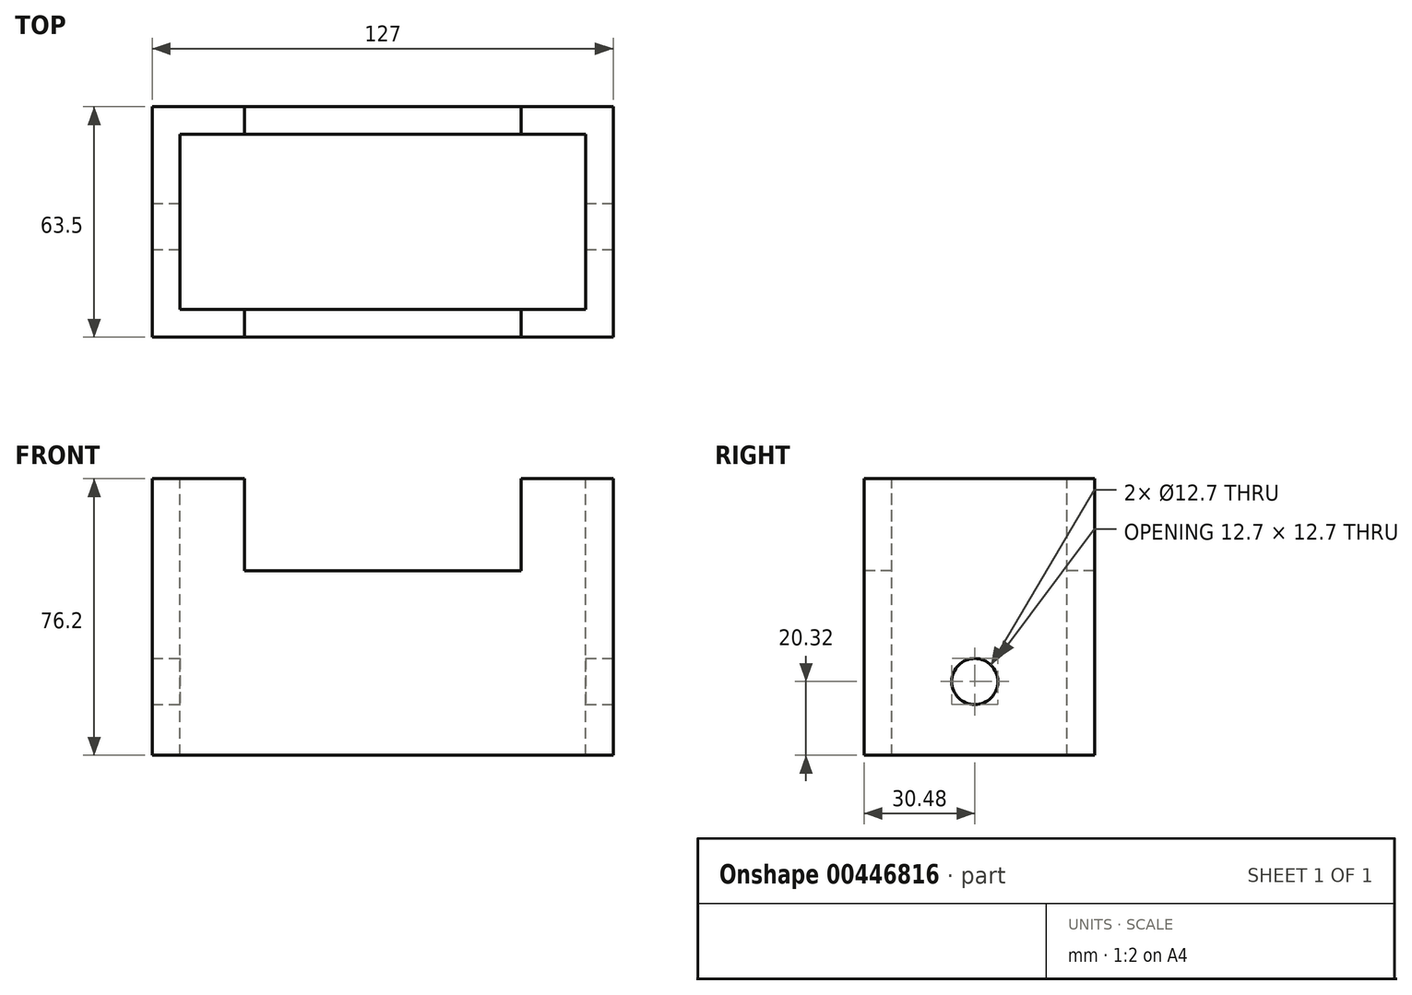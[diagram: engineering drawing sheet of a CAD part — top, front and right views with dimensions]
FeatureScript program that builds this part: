
annotation { "Feature Type Name" : "Feature", "Feature Type Description" : "" }
export const myFeature = defineFeature(function(context is Context, id is Id, definition is map)
    precondition{}
    {
        {
            var Q0;
            Q0=qCreatedBy(makeId("Front.planeOp"),FACE);
            var sketch = newSketch(context, id + "F0", { "sketchPlane" : qUnion([Q0])});
            skLineSegment(sketch, "E0.bottom", {"start": v(-63.5, 38.1) * mm, "end": v(63.5, 38.1) * mm});
            skLineSegment(sketch, "E0.top", {"start": v(-63.5, -38.1) * mm, "end": v(63.5, -38.1) * mm});
            skLineSegment(sketch, "E0.left", {"start": v(-63.5, 38.1) * mm, "end": v(-63.5, -38.1) * mm});
            skLineSegment(sketch, "E0.right", {"start": v(63.5, 38.1) * mm, "end": v(63.5, -38.1) * mm});
            skSolve(sketch);
        }
        {
            var Q0;
            Q0 = qSketchRegion(id + "F0", true);
            extrude(context, id + "F1", {"entities" : qUnion([Q0]), "depth" : 63.5 * mm});
        }
        {
            var Q0;
            Q0=makeQuery(id+"F1.opExtrude","CAP_FACE",FACE,{"disambiguationData":[OSD([sQuery(id+"F0.wireOp",EDGE,"E0.bottom"),sQuery(id+"F0.wireOp",EDGE,"E0.top"),sQuery(id+"F0.wireOp",EDGE,"E0.left"),sQuery(id+"F0.wireOp",EDGE,"E0.right")])],"isStart":false});
            var sketch = newSketch(context, id + "F2", { "sketchPlane" : qUnion([Q0])});
            skLineSegment(sketch, "E1.bottom", {"start": v(-38.1, 38.1) * mm, "end": v(38.1, 38.1) * mm});
            skLineSegment(sketch, "E1.top", {"start": v(-38.1, 12.7) * mm, "end": v(38.1, 12.7) * mm});
            skLineSegment(sketch, "E1.left", {"start": v(-38.1, 38.1) * mm, "end": v(-38.1, 12.7) * mm});
            skLineSegment(sketch, "E1.right", {"start": v(38.1, 38.1) * mm, "end": v(38.1, 12.7) * mm});
            skSolve(sketch);
        }
        {
            var Q0;
            Q0 = qSketchRegion(id + "F2", true);
            extrude(context, id + "F3", {"entities" : qUnion([Q0]), "operationType" : NewBodyOperationType.REMOVE, "oppositeDirection" : true, "depth" : 75.18 * mm});
        }
        {
            var Q0;
            {var subQ1=sQuery(id+"F0.wireOp",EDGE,"E0.left");var subQ3=sQuery(id+"F0.wireOp",EDGE,"E0.bottom");Q0=makeQuery(id+"F3.boolean.opBoolean","SPLIT",FACE,{"disambiguationData":[TD([makeQuery(id+"F1.opExtrude","SWEPT_FACE",FACE,{"disambiguationData":[OSD([subQ1])]})])],"derivedFrom":makeQuery(id+"F1.opExtrude","SWEPT_FACE",FACE,{"disambiguationData":[OSD([subQ3])]})});}
            var sketch = newSketch(context, id + "F4", { "sketchPlane" : qUnion([Q0])});
            skLineSegment(sketch, "E2.bottom", {"start": v(-55.88, -7.62) * mm, "end": v(55.88, -7.62) * mm});
            skLineSegment(sketch, "E2.top", {"start": v(-55.88, -55.88) * mm, "end": v(55.88, -55.88) * mm});
            skLineSegment(sketch, "E2.left", {"start": v(-55.88, -7.62) * mm, "end": v(-55.88, -55.88) * mm});
            skLineSegment(sketch, "E2.right", {"start": v(55.88, -7.62) * mm, "end": v(55.88, -55.88) * mm});
            skSolve(sketch);
        }
        {
            var Q0;
            Q0 = qSketchRegion(id + "F4", true);
            extrude(context, id + "F5", {"entities" : qUnion([Q0]), "operationType" : NewBodyOperationType.REMOVE, "oppositeDirection" : true, "depth" : 86.87 * mm});
        }
        {
            var Q0;
            Q0=makeQuery(id+"F1.opExtrude","SWEPT_FACE",FACE,{"disambiguationData":[OSD([sQuery(id+"F0.wireOp",EDGE,"E0.right")])]});
            var sketch = newSketch(context, id + "F6", { "sketchPlane" : qUnion([Q0])});
            skCircle(sketch, "E3", {"center": v(-33.02, -17.78) * mm, "radius": 6.35 * mm});
            skSolve(sketch);
        }
        {
            var Q0;
            Q0 = qSketchRegion(id + "F6", true);
            extrude(context, id + "F7", {"entities" : qUnion([Q0]), "operationType" : NewBodyOperationType.REMOVE, "oppositeDirection" : true, "depth" : 142.75 * mm});
        }
    });
